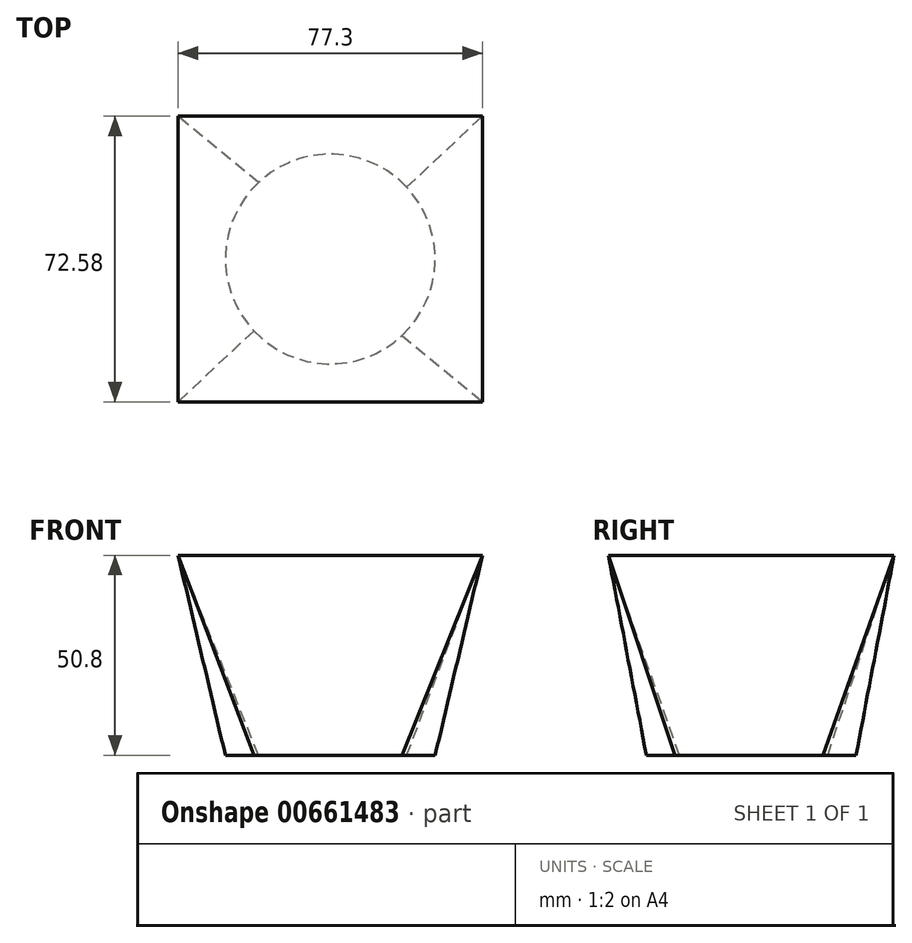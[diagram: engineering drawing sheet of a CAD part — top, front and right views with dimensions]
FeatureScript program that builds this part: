
annotation { "Feature Type Name" : "Feature", "Feature Type Description" : "" }
export const myFeature = defineFeature(function(context is Context, id is Id, definition is map)
    precondition{}
    {
        {
            var Q0;
            Q0=qCreatedBy(makeId("Top.planeOp"),FACE);
            cPlane(context, id + "F0", {"entities" : qUnion([Q0]), "cplaneType" : CPlaneType.OFFSET, "offset" : 50.8 * mm, "width" : 152.4 * mm, "height" : 152.4 * mm});
        }
        {
            var Q0;
            Q0=qCreatedBy(makeId("Top.planeOp"),FACE);
            var sketch = newSketch(context, id + "F1", { "sketchPlane" : qUnion([Q0])});
            skCircle(sketch, "E0", {"center": v(0, 0) * mm, "radius": 26.65 * mm});
            skSolve(sketch);
        }
        {
            var Q0;
            Q0=qCreatedBy(id+"F0.planeOp",FACE);
            var sketch = newSketch(context, id + "F2", { "sketchPlane" : qUnion([Q0])});
            skLineSegment(sketch, "E1.bottom", {"start": v(38.65, 36.29) * mm, "end": v(-38.65, 36.29) * mm});
            skLineSegment(sketch, "E1.top", {"start": v(38.65, -36.29) * mm, "end": v(-38.65, -36.29) * mm});
            skLineSegment(sketch, "E1.left", {"start": v(38.65, 36.29) * mm, "end": v(38.65, -36.29) * mm});
            skLineSegment(sketch, "E1.right", {"start": v(-38.65, 36.29) * mm, "end": v(-38.65, -36.29) * mm});
            skPoint(sketch, "E1.middle", {"position": v(0, 0) * mm});
            skSolve(sketch);
        }
        {
            var Q0;
            Q0=makeQuery(id+"F1.imprint","IMPRINT",FACE,{"disambiguationData":[TD([[makeQuery(id+"F1.imprint","IMPRINT",EDGE,{"derivedFrom":sQuery(id+"F1.wireOp",EDGE,"E0")}),1.0]])]});
            var Q1;
            Q1=makeQuery(id+"F2.imprint","IMPRINT",FACE,{"disambiguationData":[TD([[makeQuery(id+"F2.imprint","IMPRINT",EDGE,{"derivedFrom":sQuery(id+"F2.wireOp",EDGE,"E1.bottom")}),1.0]])]});
            loft(context, id + "F3", {"sheetProfilesArray" : [{ "sheetProfileEntities" : qUnion([Q0]) }, { "sheetProfileEntities" : qUnion([Q1]) }]});
        }
    });
